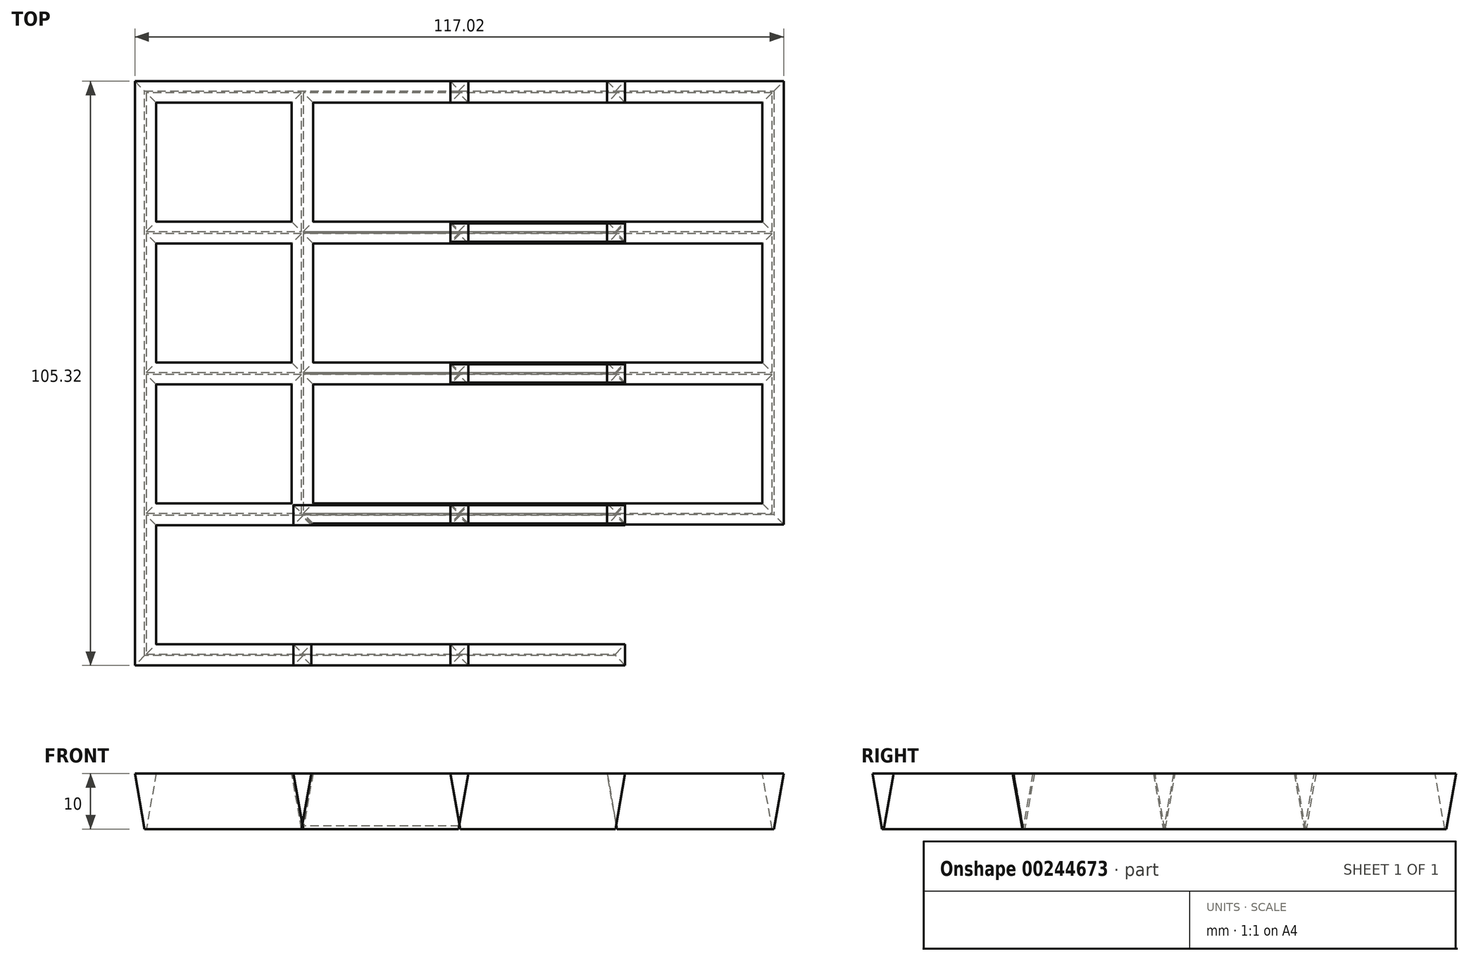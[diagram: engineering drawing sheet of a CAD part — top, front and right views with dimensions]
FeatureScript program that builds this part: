
annotation { "Feature Type Name" : "Feature", "Feature Type Description" : "" }
export const myFeature = defineFeature(function(context is Context, id is Id, definition is map)
    precondition{}
    {
        {
            var Q0;
            Q0=qCreatedBy(makeId("Top.planeOp"),FACE);
            var sketch = newSketch(context, id + "F0", { "sketchPlane" : qUnion([Q0])});
            skLineSegment(sketch, "E0.bottom", {"start": v(0, 0) * mm, "end": v(28, 0) * mm});
            skLineSegment(sketch, "E0.top", {"start": v(0, 25) * mm, "end": v(28, 25) * mm});
            skLineSegment(sketch, "E0.left", {"start": v(0, 0) * mm, "end": v(0, 25) * mm});
            skLineSegment(sketch, "E0.right", {"start": v(28, 0) * mm, "end": v(28, 25) * mm});
            skLineSegment(sketch, "E1.0", {"start": v(-0.3, -0.3) * mm, "end": v(-0.3, 25.3) * mm});
            skLineSegment(sketch, "E1.1", {"start": v(-0.3, -0.3) * mm, "end": v(28.3, -0.3) * mm});
            skLineSegment(sketch, "E1.2", {"start": v(28.3, -0.3) * mm, "end": v(28.3, 25.3) * mm});
            skLineSegment(sketch, "E1.3", {"start": v(-0.3, 25.3) * mm, "end": v(28.3, 25.3) * mm});
            skLineSegment(sketch, "E2.0.1.0", {"start": v(-0.3, 50.7) * mm, "end": v(28.3, 50.7) * mm});
            skLineSegment(sketch, "E2.0.1.1", {"start": v(28.3, 25.1) * mm, "end": v(28.3, 50.7) * mm});
            skLineSegment(sketch, "E2.0.1.2", {"start": v(-0.3, 25.1) * mm, "end": v(28.3, 25.1) * mm});
            skLineSegment(sketch, "E2.0.1.3", {"start": v(-0.3, 25.1) * mm, "end": v(-0.3, 50.7) * mm});
            skLineSegment(sketch, "E2.0.1.4", {"start": v(28, 25.4) * mm, "end": v(28, 50.4) * mm});
            skLineSegment(sketch, "E2.0.1.5", {"start": v(0, 25.4) * mm, "end": v(0, 50.4) * mm});
            skLineSegment(sketch, "E2.0.1.6", {"start": v(0, 50.4) * mm, "end": v(28, 50.4) * mm});
            skLineSegment(sketch, "E2.0.1.7", {"start": v(0, 25.4) * mm, "end": v(28, 25.4) * mm});
            skLineSegment(sketch, "E2.0.2.0", {"start": v(-0.3, 76.1) * mm, "end": v(28.3, 76.1) * mm});
            skLineSegment(sketch, "E2.0.2.1", {"start": v(28.3, 50.5) * mm, "end": v(28.3, 76.1) * mm});
            skLineSegment(sketch, "E2.0.2.2", {"start": v(-0.3, 50.5) * mm, "end": v(28.3, 50.5) * mm});
            skLineSegment(sketch, "E2.0.2.3", {"start": v(-0.3, 50.5) * mm, "end": v(-0.3, 76.1) * mm});
            skLineSegment(sketch, "E2.0.2.4", {"start": v(28, 50.8) * mm, "end": v(28, 75.8) * mm});
            skLineSegment(sketch, "E2.0.2.5", {"start": v(0, 50.8) * mm, "end": v(0, 75.8) * mm});
            skLineSegment(sketch, "E2.0.2.6", {"start": v(0, 75.8) * mm, "end": v(28, 75.8) * mm});
            skLineSegment(sketch, "E2.0.2.7", {"start": v(0, 50.8) * mm, "end": v(28, 50.8) * mm});
            skLineSegment(sketch, "E2.0.3.0", {"start": v(-0.3, 101.5) * mm, "end": v(28.3, 101.5) * mm});
            skLineSegment(sketch, "E2.0.3.1", {"start": v(28.3, 75.9) * mm, "end": v(28.3, 101.5) * mm});
            skLineSegment(sketch, "E2.0.3.2", {"start": v(-0.3, 75.9) * mm, "end": v(28.3, 75.9) * mm});
            skLineSegment(sketch, "E2.0.3.3", {"start": v(-0.3, 75.9) * mm, "end": v(-0.3, 101.5) * mm});
            skLineSegment(sketch, "E2.0.3.4", {"start": v(28, 76.2) * mm, "end": v(28, 101.2) * mm});
            skLineSegment(sketch, "E2.0.3.5", {"start": v(0, 76.2) * mm, "end": v(0, 101.2) * mm});
            skLineSegment(sketch, "E2.0.3.6", {"start": v(0, 101.2) * mm, "end": v(28, 101.2) * mm});
            skLineSegment(sketch, "E2.0.3.7", {"start": v(0, 76.2) * mm, "end": v(28, 76.2) * mm});
            skLineSegment(sketch, "E2.1.0.0", {"start": v(28, 25.3) * mm, "end": v(56.6, 25.3) * mm});
            skLineSegment(sketch, "E2.1.0.1", {"start": v(56.6, -0.3) * mm, "end": v(56.6, 25.3) * mm});
            skLineSegment(sketch, "E2.1.0.2", {"start": v(28, -0.3) * mm, "end": v(56.6, -0.3) * mm});
            skLineSegment(sketch, "E2.1.0.3", {"start": v(28, -0.3) * mm, "end": v(28, 25.3) * mm});
            skLineSegment(sketch, "E2.1.0.4", {"start": v(56.3, 0) * mm, "end": v(56.3, 25) * mm});
            skLineSegment(sketch, "E2.1.0.5", {"start": v(28.3, 0) * mm, "end": v(28.3, 25) * mm});
            skLineSegment(sketch, "E2.1.0.6", {"start": v(28.3, 25) * mm, "end": v(56.3, 25) * mm});
            skLineSegment(sketch, "E2.1.0.7", {"start": v(28.3, 0) * mm, "end": v(56.3, 0) * mm});
            skLineSegment(sketch, "E2.1.1.0", {"start": v(28, 50.7) * mm, "end": v(56.6, 50.7) * mm});
            skLineSegment(sketch, "E2.1.1.1", {"start": v(56.6, 25.1) * mm, "end": v(56.6, 50.7) * mm});
            skLineSegment(sketch, "E2.1.1.2", {"start": v(28, 25.1) * mm, "end": v(56.6, 25.1) * mm});
            skLineSegment(sketch, "E2.1.1.3", {"start": v(28, 25.1) * mm, "end": v(28, 50.7) * mm});
            skLineSegment(sketch, "E2.1.1.4", {"start": v(56.3, 25.4) * mm, "end": v(56.3, 50.4) * mm});
            skLineSegment(sketch, "E2.1.1.5", {"start": v(28.3, 25.4) * mm, "end": v(28.3, 50.4) * mm});
            skLineSegment(sketch, "E2.1.1.6", {"start": v(28.3, 50.4) * mm, "end": v(56.3, 50.4) * mm});
            skLineSegment(sketch, "E2.1.1.7", {"start": v(28.3, 25.4) * mm, "end": v(56.3, 25.4) * mm});
            skLineSegment(sketch, "E2.1.2.0", {"start": v(28, 76.1) * mm, "end": v(56.6, 76.1) * mm});
            skLineSegment(sketch, "E2.1.2.1", {"start": v(56.6, 50.5) * mm, "end": v(56.6, 76.1) * mm});
            skLineSegment(sketch, "E2.1.2.2", {"start": v(28, 50.5) * mm, "end": v(56.6, 50.5) * mm});
            skLineSegment(sketch, "E2.1.2.3", {"start": v(28, 50.5) * mm, "end": v(28, 76.1) * mm});
            skLineSegment(sketch, "E2.1.2.4", {"start": v(56.3, 50.8) * mm, "end": v(56.3, 75.8) * mm});
            skLineSegment(sketch, "E2.1.2.5", {"start": v(28.3, 50.8) * mm, "end": v(28.3, 75.8) * mm});
            skLineSegment(sketch, "E2.1.2.6", {"start": v(28.3, 75.8) * mm, "end": v(56.3, 75.8) * mm});
            skLineSegment(sketch, "E2.1.2.7", {"start": v(28.3, 50.8) * mm, "end": v(56.3, 50.8) * mm});
            skLineSegment(sketch, "E2.1.3.0", {"start": v(28, 101.5) * mm, "end": v(56.6, 101.5) * mm});
            skLineSegment(sketch, "E2.1.3.1", {"start": v(56.6, 75.9) * mm, "end": v(56.6, 101.5) * mm});
            skLineSegment(sketch, "E2.1.3.2", {"start": v(28, 75.9) * mm, "end": v(56.6, 75.9) * mm});
            skLineSegment(sketch, "E2.1.3.3", {"start": v(28, 75.9) * mm, "end": v(28, 101.5) * mm});
            skLineSegment(sketch, "E2.1.3.4", {"start": v(56.3, 76.2) * mm, "end": v(56.3, 101.2) * mm});
            skLineSegment(sketch, "E2.1.3.5", {"start": v(28.3, 76.2) * mm, "end": v(28.3, 101.2) * mm});
            skLineSegment(sketch, "E2.1.3.6", {"start": v(28.3, 101.2) * mm, "end": v(56.3, 101.2) * mm});
            skLineSegment(sketch, "E2.1.3.7", {"start": v(28.3, 76.2) * mm, "end": v(56.3, 76.2) * mm});
            skLineSegment(sketch, "E2.2.0.0", {"start": v(56.3, 25.3) * mm, "end": v(84.9, 25.3) * mm});
            skLineSegment(sketch, "E2.2.0.1", {"start": v(84.9, -0.3) * mm, "end": v(84.9, 25.3) * mm});
            skLineSegment(sketch, "E2.2.0.2", {"start": v(56.3, -0.3) * mm, "end": v(84.9, -0.3) * mm});
            skLineSegment(sketch, "E2.2.0.3", {"start": v(56.3, -0.3) * mm, "end": v(56.3, 25.3) * mm});
            skLineSegment(sketch, "E2.2.0.4", {"start": v(84.6, 0) * mm, "end": v(84.6, 25) * mm});
            skLineSegment(sketch, "E2.2.0.5", {"start": v(56.6, 0) * mm, "end": v(56.6, 25) * mm});
            skLineSegment(sketch, "E2.2.0.6", {"start": v(56.6, 25) * mm, "end": v(84.6, 25) * mm});
            skLineSegment(sketch, "E2.2.0.7", {"start": v(56.6, 0) * mm, "end": v(84.6, 0) * mm});
            skLineSegment(sketch, "E2.2.1.0", {"start": v(56.3, 50.7) * mm, "end": v(84.9, 50.7) * mm});
            skLineSegment(sketch, "E2.2.1.1", {"start": v(84.9, 25.1) * mm, "end": v(84.9, 50.7) * mm});
            skLineSegment(sketch, "E2.2.1.2", {"start": v(56.3, 25.1) * mm, "end": v(84.9, 25.1) * mm});
            skLineSegment(sketch, "E2.2.1.3", {"start": v(56.3, 25.1) * mm, "end": v(56.3, 50.7) * mm});
            skLineSegment(sketch, "E2.2.1.4", {"start": v(84.6, 25.4) * mm, "end": v(84.6, 50.4) * mm});
            skLineSegment(sketch, "E2.2.1.5", {"start": v(56.6, 25.4) * mm, "end": v(56.6, 50.4) * mm});
            skLineSegment(sketch, "E2.2.1.6", {"start": v(56.6, 50.4) * mm, "end": v(84.6, 50.4) * mm});
            skLineSegment(sketch, "E2.2.1.7", {"start": v(56.6, 25.4) * mm, "end": v(84.6, 25.4) * mm});
            skLineSegment(sketch, "E2.2.2.0", {"start": v(56.3, 76.1) * mm, "end": v(84.9, 76.1) * mm});
            skLineSegment(sketch, "E2.2.2.1", {"start": v(84.9, 50.5) * mm, "end": v(84.9, 76.1) * mm});
            skLineSegment(sketch, "E2.2.2.2", {"start": v(56.3, 50.5) * mm, "end": v(84.9, 50.5) * mm});
            skLineSegment(sketch, "E2.2.2.3", {"start": v(56.3, 50.5) * mm, "end": v(56.3, 76.1) * mm});
            skLineSegment(sketch, "E2.2.2.4", {"start": v(84.6, 50.8) * mm, "end": v(84.6, 75.8) * mm});
            skLineSegment(sketch, "E2.2.2.5", {"start": v(56.6, 50.8) * mm, "end": v(56.6, 75.8) * mm});
            skLineSegment(sketch, "E2.2.2.6", {"start": v(56.6, 75.8) * mm, "end": v(84.6, 75.8) * mm});
            skLineSegment(sketch, "E2.2.2.7", {"start": v(56.6, 50.8) * mm, "end": v(84.6, 50.8) * mm});
            skLineSegment(sketch, "E2.2.3.0", {"start": v(56.3, 101.5) * mm, "end": v(84.9, 101.5) * mm});
            skLineSegment(sketch, "E2.2.3.1", {"start": v(84.9, 75.9) * mm, "end": v(84.9, 101.5) * mm});
            skLineSegment(sketch, "E2.2.3.2", {"start": v(56.3, 75.9) * mm, "end": v(84.9, 75.9) * mm});
            skLineSegment(sketch, "E2.2.3.3", {"start": v(56.3, 75.9) * mm, "end": v(56.3, 101.5) * mm});
            skLineSegment(sketch, "E2.2.3.4", {"start": v(84.6, 76.2) * mm, "end": v(84.6, 101.2) * mm});
            skLineSegment(sketch, "E2.2.3.5", {"start": v(56.6, 76.2) * mm, "end": v(56.6, 101.2) * mm});
            skLineSegment(sketch, "E2.2.3.6", {"start": v(56.6, 101.2) * mm, "end": v(84.6, 101.2) * mm});
            skLineSegment(sketch, "E2.2.3.7", {"start": v(56.6, 76.2) * mm, "end": v(84.6, 76.2) * mm});
            skLineSegment(sketch, "E2.3.0.0", {"start": v(84.6, 25.3) * mm, "end": v(113.2, 25.3) * mm});
            skLineSegment(sketch, "E2.3.0.1", {"start": v(113.2, -0.3) * mm, "end": v(113.2, 25.3) * mm});
            skLineSegment(sketch, "E2.3.0.2", {"start": v(84.6, -0.3) * mm, "end": v(113.2, -0.3) * mm});
            skLineSegment(sketch, "E2.3.0.3", {"start": v(84.6, -0.3) * mm, "end": v(84.6, 25.3) * mm});
            skLineSegment(sketch, "E2.3.0.4", {"start": v(112.9, 0) * mm, "end": v(112.9, 25) * mm});
            skLineSegment(sketch, "E2.3.0.5", {"start": v(84.9, 0) * mm, "end": v(84.9, 25) * mm});
            skLineSegment(sketch, "E2.3.0.6", {"start": v(84.9, 25) * mm, "end": v(112.9, 25) * mm});
            skLineSegment(sketch, "E2.3.0.7", {"start": v(84.9, 0) * mm, "end": v(112.9, 0) * mm});
            skLineSegment(sketch, "E2.3.1.0", {"start": v(84.6, 50.7) * mm, "end": v(113.2, 50.7) * mm});
            skLineSegment(sketch, "E2.3.1.1", {"start": v(113.2, 25.1) * mm, "end": v(113.2, 50.7) * mm});
            skLineSegment(sketch, "E2.3.1.2", {"start": v(84.6, 25.1) * mm, "end": v(113.2, 25.1) * mm});
            skLineSegment(sketch, "E2.3.1.3", {"start": v(84.6, 25.1) * mm, "end": v(84.6, 50.7) * mm});
            skLineSegment(sketch, "E2.3.1.4", {"start": v(112.9, 25.4) * mm, "end": v(112.9, 50.4) * mm});
            skLineSegment(sketch, "E2.3.1.5", {"start": v(84.9, 25.4) * mm, "end": v(84.9, 50.4) * mm});
            skLineSegment(sketch, "E2.3.1.6", {"start": v(84.9, 50.4) * mm, "end": v(112.9, 50.4) * mm});
            skLineSegment(sketch, "E2.3.1.7", {"start": v(84.9, 25.4) * mm, "end": v(112.9, 25.4) * mm});
            skLineSegment(sketch, "E2.3.2.0", {"start": v(84.6, 76.1) * mm, "end": v(113.2, 76.1) * mm});
            skLineSegment(sketch, "E2.3.2.1", {"start": v(113.2, 50.5) * mm, "end": v(113.2, 76.1) * mm});
            skLineSegment(sketch, "E2.3.2.2", {"start": v(84.6, 50.5) * mm, "end": v(113.2, 50.5) * mm});
            skLineSegment(sketch, "E2.3.2.3", {"start": v(84.6, 50.5) * mm, "end": v(84.6, 76.1) * mm});
            skLineSegment(sketch, "E2.3.2.4", {"start": v(112.9, 50.8) * mm, "end": v(112.9, 75.8) * mm});
            skLineSegment(sketch, "E2.3.2.5", {"start": v(84.9, 50.8) * mm, "end": v(84.9, 75.8) * mm});
            skLineSegment(sketch, "E2.3.2.6", {"start": v(84.9, 75.8) * mm, "end": v(112.9, 75.8) * mm});
            skLineSegment(sketch, "E2.3.2.7", {"start": v(84.9, 50.8) * mm, "end": v(112.9, 50.8) * mm});
            skLineSegment(sketch, "E2.3.3.0", {"start": v(84.6, 101.5) * mm, "end": v(113.2, 101.5) * mm});
            skLineSegment(sketch, "E2.3.3.1", {"start": v(113.2, 75.9) * mm, "end": v(113.2, 101.5) * mm});
            skLineSegment(sketch, "E2.3.3.2", {"start": v(84.6, 75.9) * mm, "end": v(113.2, 75.9) * mm});
            skLineSegment(sketch, "E2.3.3.3", {"start": v(84.6, 75.9) * mm, "end": v(84.6, 101.5) * mm});
            skLineSegment(sketch, "E2.3.3.4", {"start": v(112.9, 76.2) * mm, "end": v(112.9, 101.2) * mm});
            skLineSegment(sketch, "E2.3.3.5", {"start": v(84.9, 76.2) * mm, "end": v(84.9, 101.2) * mm});
            skLineSegment(sketch, "E2.3.3.6", {"start": v(84.9, 101.2) * mm, "end": v(112.9, 101.2) * mm});
            skLineSegment(sketch, "E2.3.3.7", {"start": v(84.9, 76.2) * mm, "end": v(112.9, 76.2) * mm});
            skLineSegment(sketch, "E2.direction1", {"start": v(-0.3, -0.3) * mm, "end": v(28, -0.3) * mm, "construction": true});
            skLineSegment(sketch, "E2.direction2", {"start": v(-0.3, -0.3) * mm, "end": v(-0.3, 25.1) * mm, "construction": true});
            skSolve(sketch);
        }
        {
            var Q0;
            {var subQ3=sQuery(id+"F0.wireOp",EDGE,"E0.bottom");Q0=makeQuery(id+"F0.imprint","IMPRINT",FACE,{"disambiguationData":[TD([[makeQuery(id+"F0.imprint","IMPRINT",EDGE,{"derivedFrom":subQ3}),-1.0]])]});}
            var Q1;
            {var subQ3=sQuery(id+"F0.wireOp",EDGE,"E2.1.0.7");Q1=makeQuery(id+"F0.imprint","IMPRINT",FACE,{"disambiguationData":[TD([[makeQuery(id+"F0.imprint","IMPRINT",EDGE,{"derivedFrom":subQ3}),-1.0]])]});}
            var Q2;
            {var subQ0=sQuery(id+"F0.wireOp",EDGE,"E1.3");Q2=makeQuery(id+"F0.imprint","IMPRINT",FACE,{"disambiguationData":[TD([[makeQuery(id+"F0.imprint","IMPRINT",EDGE,{"derivedFrom":subQ0}),-1.0]])]});}
            var Q3;
            {var subQ0=sQuery(id+"F0.wireOp",EDGE,"E2.0.1.0");Q3=makeQuery(id+"F0.imprint","IMPRINT",FACE,{"disambiguationData":[TD([[makeQuery(id+"F0.imprint","IMPRINT",EDGE,{"derivedFrom":subQ0}),-1.0]])]});}
            var Q4;
            {var subQ1=sQuery(id+"F0.wireOp",EDGE,"E2.0.2.0");Q4=makeQuery(id+"F0.imprint","IMPRINT",FACE,{"disambiguationData":[TD([[makeQuery(id+"F0.imprint","IMPRINT",EDGE,{"derivedFrom":subQ1}),1.0]])]});}
            var Q5;
            {var subQ0=sQuery(id+"F0.wireOp",EDGE,"E2.0.2.0");Q5=makeQuery(id+"F0.imprint","IMPRINT",FACE,{"disambiguationData":[TD([[makeQuery(id+"F0.imprint","IMPRINT",EDGE,{"derivedFrom":subQ0}),-1.0]])]});}
            var Q6;
            {var subQ3=sQuery(id+"F0.wireOp",EDGE,"E2.1.3.6");Q6=makeQuery(id+"F0.imprint","IMPRINT",FACE,{"disambiguationData":[TD([[makeQuery(id+"F0.imprint","IMPRINT",EDGE,{"derivedFrom":subQ3}),1.0]])]});}
            var Q7;
            {var subQ3=sQuery(id+"F0.wireOp",EDGE,"E2.2.0.7");Q7=makeQuery(id+"F0.imprint","IMPRINT",FACE,{"disambiguationData":[TD([[makeQuery(id+"F0.imprint","IMPRINT",EDGE,{"derivedFrom":subQ3}),-1.0]])]});}
            var Q8;
            {var subQ3=sQuery(id+"F0.wireOp",EDGE,"E2.2.3.6");Q8=makeQuery(id+"F0.imprint","IMPRINT",FACE,{"disambiguationData":[TD([[makeQuery(id+"F0.imprint","IMPRINT",EDGE,{"derivedFrom":subQ3}),1.0]])]});}
            var Q9;
            {var subQ3=sQuery(id+"F0.wireOp",EDGE,"E2.3.0.1");Q9=makeQuery(id+"F0.imprint","IMPRINT",FACE,{"disambiguationData":[TD([[makeQuery(id+"F0.imprint","IMPRINT",EDGE,{"derivedFrom":subQ3}),1.0]])]});}
            var Q10;
            {var subQ3=sQuery(id+"F0.wireOp",EDGE,"E2.3.0.0");var subQ5=sQuery(id+"F0.wireOp",EDGE,"E2.3.1.1");var subQ6=makeQuery(id+"F0.imprint","INTERSECT",VERTEX,{"derivedFrom":[subQ3,subQ5]});Q10=makeQuery(id+"F0.imprint","IMPRINT",FACE,{"disambiguationData":[TD([[makeQuery(id+"F0.imprint","IMPRINT",EDGE,{"disambiguationData":[TD([[subQ6,1.0]])],"derivedFrom":subQ3}),-1.0]])]});}
            var Q11;
            {var subQ3=sQuery(id+"F0.wireOp",EDGE,"E2.3.1.0");var subQ5=sQuery(id+"F0.wireOp",EDGE,"E2.3.2.1");var subQ6=makeQuery(id+"F0.imprint","INTERSECT",VERTEX,{"derivedFrom":[subQ3,subQ5]});Q11=makeQuery(id+"F0.imprint","IMPRINT",FACE,{"disambiguationData":[TD([[makeQuery(id+"F0.imprint","IMPRINT",EDGE,{"disambiguationData":[TD([[subQ6,1.0]])],"derivedFrom":subQ3}),-1.0]])]});}
            var Q12;
            {var subQ3=sQuery(id+"F0.wireOp",EDGE,"E2.3.2.0");var subQ5=sQuery(id+"F0.wireOp",EDGE,"E2.3.3.1");var subQ6=makeQuery(id+"F0.imprint","INTERSECT",VERTEX,{"derivedFrom":[subQ3,subQ5]});Q12=makeQuery(id+"F0.imprint","IMPRINT",FACE,{"disambiguationData":[TD([[makeQuery(id+"F0.imprint","IMPRINT",EDGE,{"disambiguationData":[TD([[subQ6,1.0]])],"derivedFrom":subQ3}),-1.0]])]});}
            var Q13;
            Q13=makeQuery(id+"F0.imprint","IMPRINT",FACE,{"disambiguationData":[TD([[makeQuery(id+"F0.imprint","IMPRINT",EDGE,{"derivedFrom":sQuery(id+"F0.wireOp",EDGE,"E2.3.3.4")}),-1.0]])]});
            var Q14;
            {var subQ2=sQuery(id+"F0.wireOp",EDGE,"E1.3");Q14=makeQuery(id+"F0.imprint","IMPRINT",FACE,{"disambiguationData":[TD([[makeQuery(id+"F0.imprint","IMPRINT",EDGE,{"derivedFrom":subQ2}),1.0]])]});}
            var Q15;
            {var subQ2=sQuery(id+"F0.wireOp",EDGE,"E2.0.1.0");Q15=makeQuery(id+"F0.imprint","IMPRINT",FACE,{"disambiguationData":[TD([[makeQuery(id+"F0.imprint","IMPRINT",EDGE,{"derivedFrom":subQ2}),1.0]])]});}
            var Q16;
            Q16=makeQuery(id+"F0.imprint","IMPRINT",FACE,{"disambiguationData":[TD([[makeQuery(id+"F0.imprint","IMPRINT",EDGE,{"derivedFrom":sQuery(id+"F0.wireOp",EDGE,"E2.3.1.4")}),-1.0]])]});
            var Q17;
            Q17=makeQuery(id+"F0.imprint","IMPRINT",FACE,{"disambiguationData":[TD([[makeQuery(id+"F0.imprint","IMPRINT",EDGE,{"derivedFrom":sQuery(id+"F0.wireOp",EDGE,"E2.3.2.4")}),-1.0]])]});
            var Q18;
            {var subQ7=sQuery(id+"F0.wireOp",EDGE,"E2.1.0.5");Q18=makeQuery(id+"F0.imprint","IMPRINT",FACE,{"disambiguationData":[TD([[makeQuery(id+"F0.imprint","IMPRINT",EDGE,{"derivedFrom":subQ7}),1.0]])]});}
            var Q19;
            {var subQ5=sQuery(id+"F0.wireOp",EDGE,"E2.1.3.5");Q19=makeQuery(id+"F0.imprint","IMPRINT",FACE,{"disambiguationData":[TD([[makeQuery(id+"F0.imprint","IMPRINT",EDGE,{"derivedFrom":subQ5}),1.0]])]});}
            var Q20;
            {var subQ7=sQuery(id+"F0.wireOp",EDGE,"E2.3.0.5");Q20=makeQuery(id+"F0.imprint","IMPRINT",FACE,{"disambiguationData":[TD([[makeQuery(id+"F0.imprint","IMPRINT",EDGE,{"derivedFrom":subQ7}),1.0]])]});}
            var Q21;
            {var subQ9=sQuery(id+"F0.wireOp",EDGE,"E2.3.3.5");Q21=makeQuery(id+"F0.imprint","IMPRINT",FACE,{"disambiguationData":[TD([[makeQuery(id+"F0.imprint","IMPRINT",EDGE,{"derivedFrom":subQ9}),1.0]])]});}
            var Q22;
            {var subQ8=sQuery(id+"F0.wireOp",EDGE,"E2.2.0.5");Q22=makeQuery(id+"F0.imprint","IMPRINT",FACE,{"disambiguationData":[TD([[makeQuery(id+"F0.imprint","IMPRINT",EDGE,{"derivedFrom":subQ8}),1.0]])]});}
            var Q23;
            {var subQ9=sQuery(id+"F0.wireOp",EDGE,"E2.2.3.5");Q23=makeQuery(id+"F0.imprint","IMPRINT",FACE,{"disambiguationData":[TD([[makeQuery(id+"F0.imprint","IMPRINT",EDGE,{"derivedFrom":subQ9}),1.0]])]});}
            var Q24;
            {var subQ0=sQuery(id+"F0.wireOp",EDGE,"E2.1.1.7");Q24=makeQuery(id+"F0.imprint","IMPRINT",FACE,{"disambiguationData":[TD([[makeQuery(id+"F0.imprint","IMPRINT",EDGE,{"derivedFrom":subQ0}),-1.0]])]});}
            var Q25;
            {var subQ0=sQuery(id+"F0.wireOp",EDGE,"E2.2.1.7");Q25=makeQuery(id+"F0.imprint","IMPRINT",FACE,{"disambiguationData":[TD([[makeQuery(id+"F0.imprint","IMPRINT",EDGE,{"derivedFrom":subQ0}),-1.0]])]});}
            var Q26;
            {var subQ9=sQuery(id+"F0.wireOp",EDGE,"E2.1.1.5");Q26=makeQuery(id+"F0.imprint","IMPRINT",FACE,{"disambiguationData":[TD([[makeQuery(id+"F0.imprint","IMPRINT",EDGE,{"derivedFrom":subQ9}),1.0]])]});}
            var Q27;
            {var subQ8=sQuery(id+"F0.wireOp",EDGE,"E2.1.2.5");Q27=makeQuery(id+"F0.imprint","IMPRINT",FACE,{"disambiguationData":[TD([[makeQuery(id+"F0.imprint","IMPRINT",EDGE,{"derivedFrom":subQ8}),1.0]])]});}
            var Q28;
            {var subQ1=sQuery(id+"F0.wireOp",EDGE,"E2.0.1.1");var subQ3=sQuery(id+"F0.wireOp",EDGE,"E2.1.0.0");var subQ4=makeQuery(id+"F0.imprint","INTERSECT",VERTEX,{"derivedFrom":[subQ1,subQ3]});Q28=makeQuery(id+"F0.imprint","IMPRINT",FACE,{"disambiguationData":[TD([[makeQuery(id+"F0.imprint","IMPRINT",EDGE,{"disambiguationData":[TD([[subQ4,1.0]])],"derivedFrom":subQ1}),-1.0]])]});}
            var Q29;
            {var subQ3=sQuery(id+"F0.wireOp",EDGE,"E2.2.0.6");Q29=makeQuery(id+"F0.imprint","IMPRINT",FACE,{"disambiguationData":[TD([[makeQuery(id+"F0.imprint","IMPRINT",EDGE,{"derivedFrom":subQ3}),1.0]])]});}
            var Q30;
            {var subQ0=sQuery(id+"F0.wireOp",EDGE,"E2.2.2.7");Q30=makeQuery(id+"F0.imprint","IMPRINT",FACE,{"disambiguationData":[TD([[makeQuery(id+"F0.imprint","IMPRINT",EDGE,{"derivedFrom":subQ0}),-1.0]])]});}
            var Q31;
            {var subQ3=sQuery(id+"F0.wireOp",EDGE,"E2.2.2.6");Q31=makeQuery(id+"F0.imprint","IMPRINT",FACE,{"disambiguationData":[TD([[makeQuery(id+"F0.imprint","IMPRINT",EDGE,{"derivedFrom":subQ3}),1.0]])]});}
            var Q32;
            {var subQ1=sQuery(id+"F0.wireOp",EDGE,"E2.0.2.1");var subQ3=sQuery(id+"F0.wireOp",EDGE,"E2.1.1.0");var subQ4=makeQuery(id+"F0.imprint","INTERSECT",VERTEX,{"derivedFrom":[subQ1,subQ3]});Q32=makeQuery(id+"F0.imprint","IMPRINT",FACE,{"disambiguationData":[TD([[makeQuery(id+"F0.imprint","IMPRINT",EDGE,{"disambiguationData":[TD([[subQ4,1.0]])],"derivedFrom":subQ1}),-1.0]])]});}
            var Q33;
            {var subQ3=sQuery(id+"F0.wireOp",EDGE,"E2.1.2.6");Q33=makeQuery(id+"F0.imprint","IMPRINT",FACE,{"disambiguationData":[TD([[makeQuery(id+"F0.imprint","IMPRINT",EDGE,{"derivedFrom":subQ3}),1.0]])]});}
            var Q34;
            {var subQ4=sQuery(id+"F0.wireOp",EDGE,"E2.3.1.5");Q34=makeQuery(id+"F0.imprint","IMPRINT",FACE,{"disambiguationData":[TD([[makeQuery(id+"F0.imprint","IMPRINT",EDGE,{"derivedFrom":subQ4}),1.0]])]});}
            var Q35;
            {var subQ4=sQuery(id+"F0.wireOp",EDGE,"E2.3.2.5");Q35=makeQuery(id+"F0.imprint","IMPRINT",FACE,{"disambiguationData":[TD([[makeQuery(id+"F0.imprint","IMPRINT",EDGE,{"derivedFrom":subQ4}),1.0]])]});}
            var Q36;
            {var subQ3=sQuery(id+"F0.wireOp",EDGE,"E2.1.0.6");Q36=makeQuery(id+"F0.imprint","IMPRINT",FACE,{"disambiguationData":[TD([[makeQuery(id+"F0.imprint","IMPRINT",EDGE,{"derivedFrom":subQ3}),1.0]])]});}
            var Q37;
            {var subQ1=sQuery(id+"F0.wireOp",EDGE,"E2.1.1.1");var subQ3=sQuery(id+"F0.wireOp",EDGE,"E2.2.0.0");var subQ4=makeQuery(id+"F0.imprint","INTERSECT",VERTEX,{"derivedFrom":[subQ1,subQ3]});Q37=makeQuery(id+"F0.imprint","IMPRINT",FACE,{"disambiguationData":[TD([[makeQuery(id+"F0.imprint","IMPRINT",EDGE,{"disambiguationData":[TD([[subQ4,1.0]])],"derivedFrom":subQ1}),-1.0]])]});}
            var Q38;
            {var subQ10=sQuery(id+"F0.wireOp",EDGE,"E2.2.1.5");Q38=makeQuery(id+"F0.imprint","IMPRINT",FACE,{"disambiguationData":[TD([[makeQuery(id+"F0.imprint","IMPRINT",EDGE,{"derivedFrom":subQ10}),1.0]])]});}
            var Q39;
            {var subQ9=sQuery(id+"F0.wireOp",EDGE,"E2.2.2.5");Q39=makeQuery(id+"F0.imprint","IMPRINT",FACE,{"disambiguationData":[TD([[makeQuery(id+"F0.imprint","IMPRINT",EDGE,{"derivedFrom":subQ9}),1.0]])]});}
            var Q40;
            {var subQ1=sQuery(id+"F0.wireOp",EDGE,"E2.1.2.1");var subQ3=sQuery(id+"F0.wireOp",EDGE,"E2.2.1.0");var subQ4=makeQuery(id+"F0.imprint","INTERSECT",VERTEX,{"derivedFrom":[subQ1,subQ3]});Q40=makeQuery(id+"F0.imprint","IMPRINT",FACE,{"disambiguationData":[TD([[makeQuery(id+"F0.imprint","IMPRINT",EDGE,{"disambiguationData":[TD([[subQ4,1.0]])],"derivedFrom":subQ1}),-1.0]])]});}
            var Q41;
            {var subQ3=sQuery(id+"F0.wireOp",EDGE,"E2.1.1.6");Q41=makeQuery(id+"F0.imprint","IMPRINT",FACE,{"disambiguationData":[TD([[makeQuery(id+"F0.imprint","IMPRINT",EDGE,{"derivedFrom":subQ3}),1.0]])]});}
            var Q42;
            {var subQ1=sQuery(id+"F0.wireOp",EDGE,"E2.1.3.1");var subQ3=sQuery(id+"F0.wireOp",EDGE,"E2.2.2.0");var subQ4=makeQuery(id+"F0.imprint","INTERSECT",VERTEX,{"derivedFrom":[subQ1,subQ3]});Q42=makeQuery(id+"F0.imprint","IMPRINT",FACE,{"disambiguationData":[TD([[makeQuery(id+"F0.imprint","IMPRINT",EDGE,{"disambiguationData":[TD([[subQ4,1.0]])],"derivedFrom":subQ1}),-1.0]])]});}
            var Q43;
            {var subQ1=sQuery(id+"F0.wireOp",EDGE,"E2.0.3.1");var subQ3=sQuery(id+"F0.wireOp",EDGE,"E2.1.2.0");var subQ4=makeQuery(id+"F0.imprint","INTERSECT",VERTEX,{"derivedFrom":[subQ1,subQ3]});Q43=makeQuery(id+"F0.imprint","IMPRINT",FACE,{"disambiguationData":[TD([[makeQuery(id+"F0.imprint","IMPRINT",EDGE,{"disambiguationData":[TD([[subQ4,1.0]])],"derivedFrom":subQ1}),-1.0]])]});}
            var Q44;
            {var subQ0=sQuery(id+"F0.wireOp",EDGE,"E2.2.3.7");Q44=makeQuery(id+"F0.imprint","IMPRINT",FACE,{"disambiguationData":[TD([[makeQuery(id+"F0.imprint","IMPRINT",EDGE,{"derivedFrom":subQ0}),-1.0]])]});}
            var Q45;
            {var subQ0=sQuery(id+"F0.wireOp",EDGE,"E2.1.3.7");Q45=makeQuery(id+"F0.imprint","IMPRINT",FACE,{"disambiguationData":[TD([[makeQuery(id+"F0.imprint","IMPRINT",EDGE,{"derivedFrom":subQ0}),-1.0]])]});}
            var Q46;
            {var subQ0=sQuery(id+"F0.wireOp",EDGE,"E2.1.2.7");Q46=makeQuery(id+"F0.imprint","IMPRINT",FACE,{"disambiguationData":[TD([[makeQuery(id+"F0.imprint","IMPRINT",EDGE,{"derivedFrom":subQ0}),-1.0]])]});}
            var Q47;
            {var subQ3=sQuery(id+"F0.wireOp",EDGE,"E2.2.1.6");Q47=makeQuery(id+"F0.imprint","IMPRINT",FACE,{"disambiguationData":[TD([[makeQuery(id+"F0.imprint","IMPRINT",EDGE,{"derivedFrom":subQ3}),1.0]])]});}
            var Q48;
            {var subQ1=sQuery(id+"F0.wireOp",EDGE,"E2.2.3.1");var subQ3=sQuery(id+"F0.wireOp",EDGE,"E2.3.2.0");var subQ4=makeQuery(id+"F0.imprint","INTERSECT",VERTEX,{"derivedFrom":[subQ1,subQ3]});Q48=makeQuery(id+"F0.imprint","IMPRINT",FACE,{"disambiguationData":[TD([[makeQuery(id+"F0.imprint","IMPRINT",EDGE,{"disambiguationData":[TD([[subQ4,1.0]])],"derivedFrom":subQ1}),1.0]])]});}
            var Q49;
            {var subQ1=sQuery(id+"F0.wireOp",EDGE,"E2.1.3.1");var subQ3=sQuery(id+"F0.wireOp",EDGE,"E2.2.2.0");var subQ4=makeQuery(id+"F0.imprint","INTERSECT",VERTEX,{"derivedFrom":[subQ1,subQ3]});Q49=makeQuery(id+"F0.imprint","IMPRINT",FACE,{"disambiguationData":[TD([[makeQuery(id+"F0.imprint","IMPRINT",EDGE,{"disambiguationData":[TD([[subQ4,1.0]])],"derivedFrom":subQ1}),1.0]])]});}
            var Q50;
            {var subQ1=sQuery(id+"F0.wireOp",EDGE,"E2.0.3.1");var subQ3=sQuery(id+"F0.wireOp",EDGE,"E2.1.2.0");var subQ4=makeQuery(id+"F0.imprint","INTERSECT",VERTEX,{"derivedFrom":[subQ1,subQ3]});Q50=makeQuery(id+"F0.imprint","IMPRINT",FACE,{"disambiguationData":[TD([[makeQuery(id+"F0.imprint","IMPRINT",EDGE,{"disambiguationData":[TD([[subQ4,1.0]])],"derivedFrom":subQ1}),1.0]])]});}
            var Q51;
            {var subQ1=sQuery(id+"F0.wireOp",EDGE,"E2.2.1.1");var subQ3=sQuery(id+"F0.wireOp",EDGE,"E2.3.0.0");var subQ4=makeQuery(id+"F0.imprint","INTERSECT",VERTEX,{"derivedFrom":[subQ1,subQ3]});Q51=makeQuery(id+"F0.imprint","IMPRINT",FACE,{"disambiguationData":[TD([[makeQuery(id+"F0.imprint","IMPRINT",EDGE,{"disambiguationData":[TD([[subQ4,1.0]])],"derivedFrom":subQ1}),1.0]])]});}
            var Q52;
            {var subQ1=sQuery(id+"F0.wireOp",EDGE,"E2.2.2.1");var subQ3=sQuery(id+"F0.wireOp",EDGE,"E2.3.1.0");var subQ4=makeQuery(id+"F0.imprint","INTERSECT",VERTEX,{"derivedFrom":[subQ1,subQ3]});Q52=makeQuery(id+"F0.imprint","IMPRINT",FACE,{"disambiguationData":[TD([[makeQuery(id+"F0.imprint","IMPRINT",EDGE,{"disambiguationData":[TD([[subQ4,1.0]])],"derivedFrom":subQ1}),1.0]])]});}
            var Q53;
            {var subQ1=sQuery(id+"F0.wireOp",EDGE,"E2.0.2.1");var subQ3=sQuery(id+"F0.wireOp",EDGE,"E2.1.1.0");var subQ4=makeQuery(id+"F0.imprint","INTERSECT",VERTEX,{"derivedFrom":[subQ1,subQ3]});Q53=makeQuery(id+"F0.imprint","IMPRINT",FACE,{"disambiguationData":[TD([[makeQuery(id+"F0.imprint","IMPRINT",EDGE,{"disambiguationData":[TD([[subQ4,1.0]])],"derivedFrom":subQ1}),1.0]])]});}
            var Q54;
            {var subQ1=sQuery(id+"F0.wireOp",EDGE,"E2.1.2.1");var subQ3=sQuery(id+"F0.wireOp",EDGE,"E2.2.1.0");var subQ4=makeQuery(id+"F0.imprint","INTERSECT",VERTEX,{"derivedFrom":[subQ1,subQ3]});Q54=makeQuery(id+"F0.imprint","IMPRINT",FACE,{"disambiguationData":[TD([[makeQuery(id+"F0.imprint","IMPRINT",EDGE,{"disambiguationData":[TD([[subQ4,1.0]])],"derivedFrom":subQ1}),1.0]])]});}
            var Q55;
            {var subQ1=sQuery(id+"F0.wireOp",EDGE,"E2.1.1.1");var subQ3=sQuery(id+"F0.wireOp",EDGE,"E2.2.0.0");var subQ4=makeQuery(id+"F0.imprint","INTERSECT",VERTEX,{"derivedFrom":[subQ1,subQ3]});Q55=makeQuery(id+"F0.imprint","IMPRINT",FACE,{"disambiguationData":[TD([[makeQuery(id+"F0.imprint","IMPRINT",EDGE,{"disambiguationData":[TD([[subQ4,1.0]])],"derivedFrom":subQ1}),1.0]])]});}
            var Q56;
            {var subQ1=sQuery(id+"F0.wireOp",EDGE,"E2.0.1.1");var subQ3=sQuery(id+"F0.wireOp",EDGE,"E2.1.0.0");var subQ4=makeQuery(id+"F0.imprint","INTERSECT",VERTEX,{"derivedFrom":[subQ1,subQ3]});Q56=makeQuery(id+"F0.imprint","IMPRINT",FACE,{"disambiguationData":[TD([[makeQuery(id+"F0.imprint","IMPRINT",EDGE,{"disambiguationData":[TD([[subQ4,1.0]])],"derivedFrom":subQ1}),1.0]])]});}
            extrude(context, id + "F1", {"entities" : qUnion([Q0, Q1, Q2, Q3, Q4, Q5, Q6, Q7, Q8, Q9, Q10, Q11, Q12, Q13, Q14, Q15, Q16, Q17, Q18, Q19, Q20, Q21, Q22, Q23, Q24, Q25, Q26, Q27, Q28, Q29, Q30, Q31, Q32, Q33, Q34, Q35, Q36, Q37, Q38, Q39, Q40, Q41, Q42, Q43, Q44, Q45, Q46, Q47, Q48, Q49, Q50, Q51, Q52, Q53, Q54, Q55, Q56]), "depth" : 10 * mm, "hasDraft" : true, "draftAngle" : 10 * degree});
        }
    });
